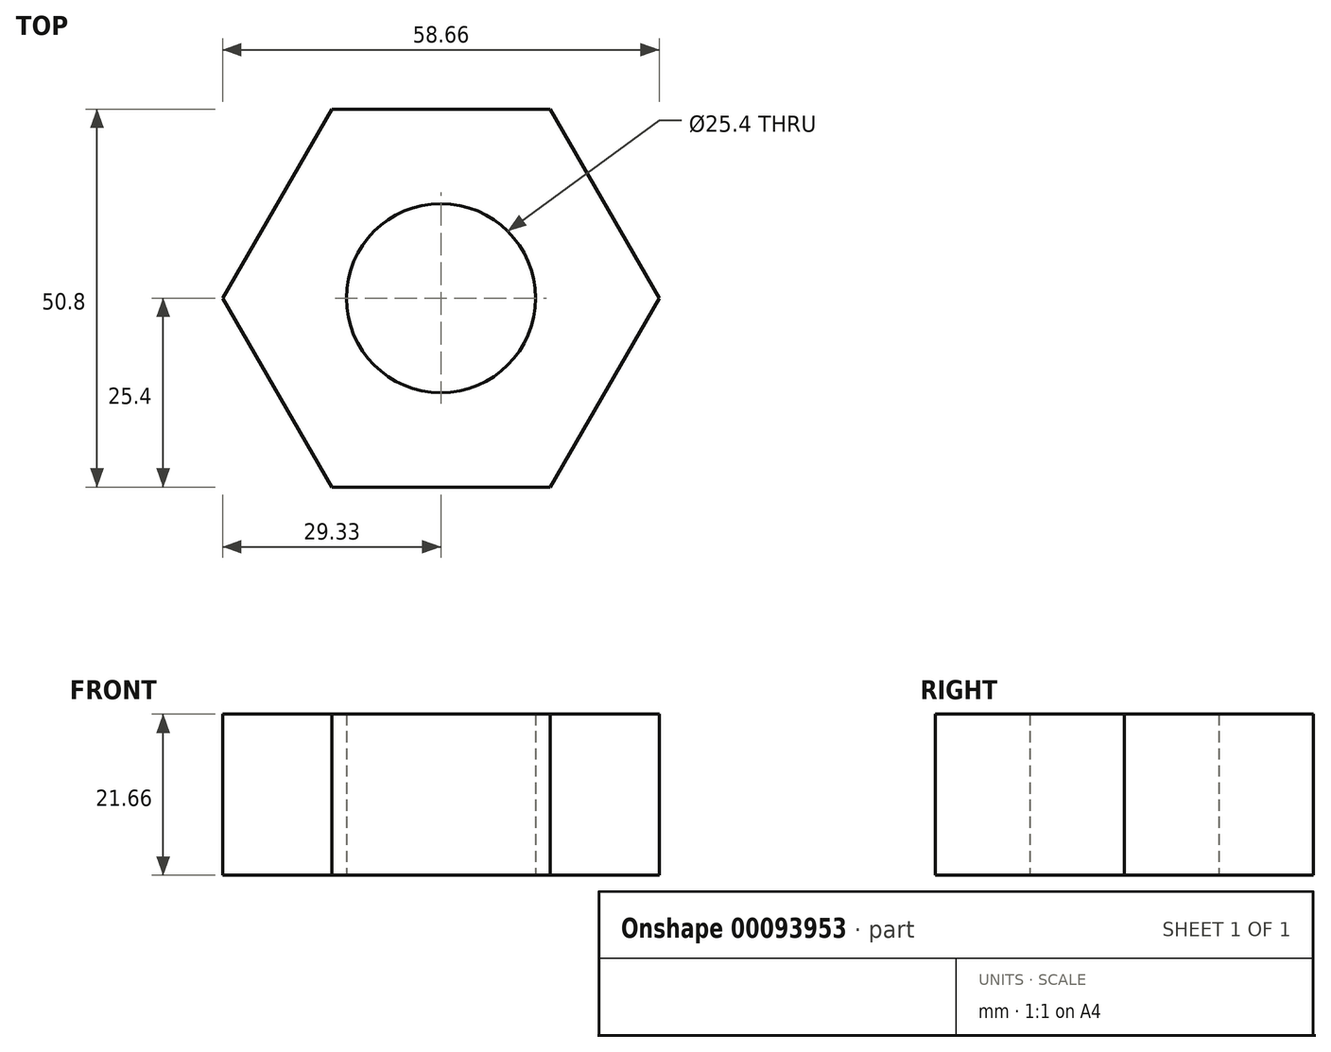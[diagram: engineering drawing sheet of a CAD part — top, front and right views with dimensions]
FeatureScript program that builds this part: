
annotation { "Feature Type Name" : "Feature", "Feature Type Description" : "" }
export const myFeature = defineFeature(function(context is Context, id is Id, definition is map)
    precondition{}
    {
        {
            var Q0;
            Q0=qCreatedBy(makeId("Top.planeOp"),FACE);
            var sketch = newSketch(context, id + "F0", { "sketchPlane" : qUnion([Q0])});
            skCircle(sketch, "E0.cCircle", {"center": v(0, 0) * mm, "radius": 25.4 * mm, "construction": true});
            skLineSegment(sketch, "E0.0", {"start": v(29.33, 0) * mm, "end": v(14.66, -25.4) * mm});
            skLineSegment(sketch, "E0.1", {"start": v(14.66, -25.4) * mm, "end": v(-14.66, -25.4) * mm});
            skLineSegment(sketch, "E0.2", {"start": v(-14.66, -25.4) * mm, "end": v(-29.33, 0) * mm});
            skLineSegment(sketch, "E0.3", {"start": v(-29.33, 0) * mm, "end": v(-14.66, 25.4) * mm});
            skLineSegment(sketch, "E0.4", {"start": v(-14.66, 25.4) * mm, "end": v(14.66, 25.4) * mm});
            skLineSegment(sketch, "E0.5", {"start": v(14.66, 25.4) * mm, "end": v(29.33, 0) * mm});
            skPoint(sketch, "E0.0.midPoint", {"position": v(22, -12.7) * mm});
            skCircle(sketch, "E1", {"center": v(0, 0) * mm, "radius": 12.7 * mm});
            skSolve(sketch);
        }
        {
            var Q0;
            Q0=makeQuery(id+"F0.imprint","IMPRINT",FACE,{"disambiguationData":[TD([[makeQuery(id+"F0.imprint","IMPRINT",EDGE,{"derivedFrom":sQuery(id+"F0.wireOp",EDGE,"E0.0")}),-1.0]])]});
            extrude(context, id + "F1", {"entities" : qUnion([Q0]), "endBound" : BoundingType.SYMMETRIC, "depth" : 21.67 * mm});
        }
    });
